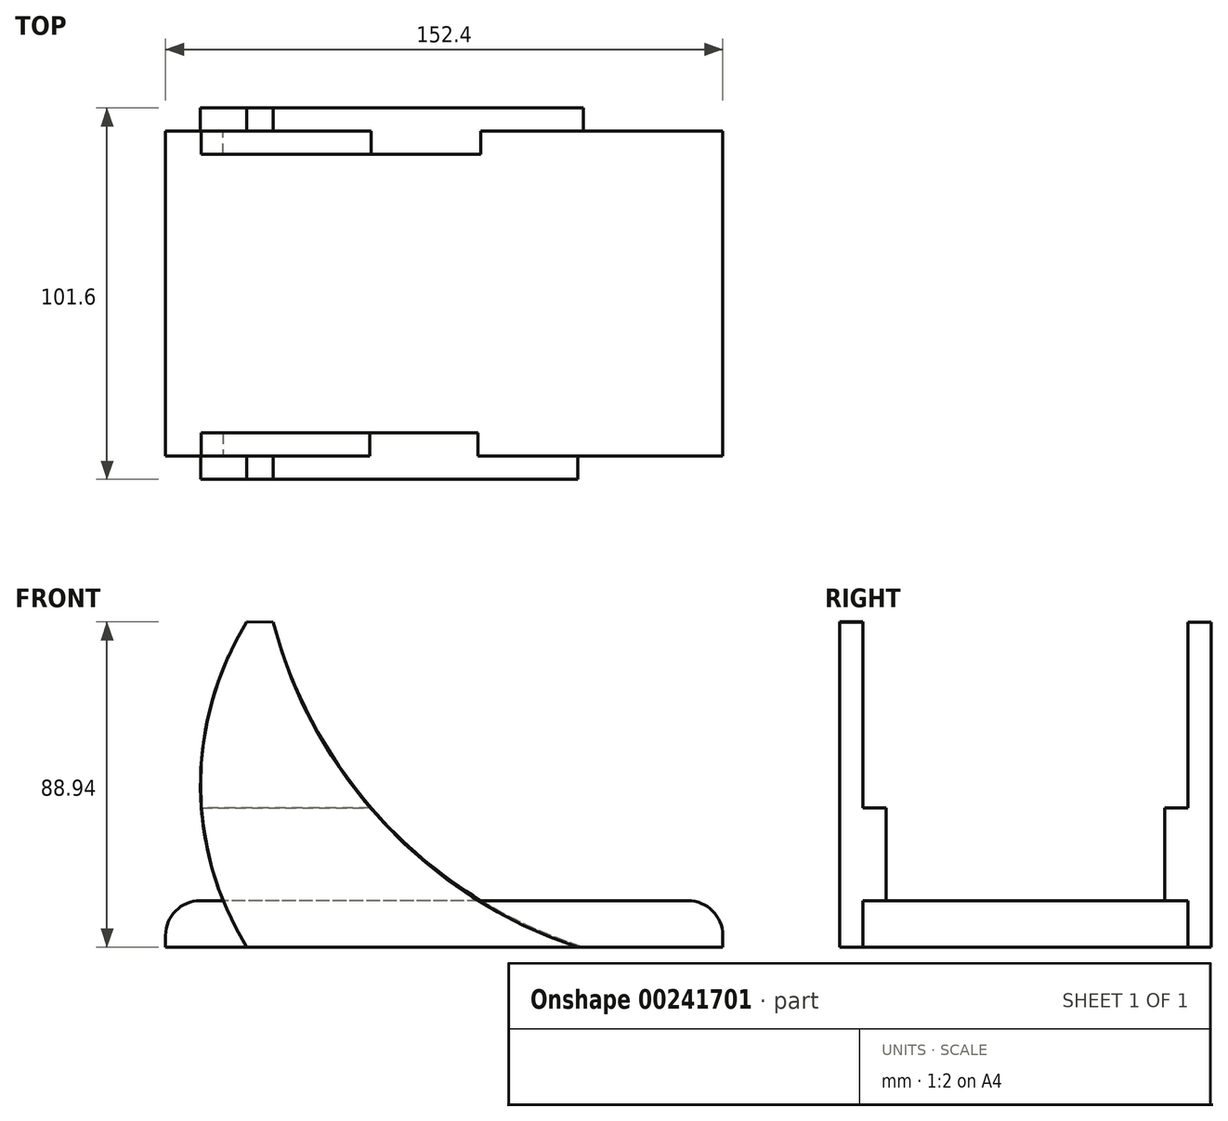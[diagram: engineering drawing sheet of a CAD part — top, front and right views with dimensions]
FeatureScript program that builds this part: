
annotation { "Feature Type Name" : "Feature", "Feature Type Description" : "" }
export const myFeature = defineFeature(function(context is Context, id is Id, definition is map)
    precondition{}
    {
        {
            var Q0;
            Q0=qCreatedBy(makeId("Top.planeOp"),FACE);
            var sketch = newSketch(context, id + "F0", { "sketchPlane" : qUnion([Q0])});
            skLineSegment(sketch, "E0.bottom", {"start": v(76.2, -44.45) * mm, "end": v(-76.2, -44.45) * mm});
            skLineSegment(sketch, "E0.top", {"start": v(76.2, 44.45) * mm, "end": v(-76.2, 44.45) * mm});
            skLineSegment(sketch, "E0.left", {"start": v(76.2, -44.45) * mm, "end": v(76.2, 44.45) * mm});
            skLineSegment(sketch, "E0.right", {"start": v(-76.2, -44.45) * mm, "end": v(-76.2, 44.45) * mm});
            skPoint(sketch, "E0.middle", {"position": v(0, 0) * mm});
            skSolve(sketch);
        }
        {
            var Q0;
            Q0=makeQuery(id+"F0.imprint","IMPRINT",FACE,{"disambiguationData":[TD([[makeQuery(id+"F0.imprint","IMPRINT",EDGE,{"derivedFrom":sQuery(id+"F0.wireOp",EDGE,"E0.bottom")}),-1.0]])]});
            extrude(context, id + "F1", {"entities" : qUnion([Q0]), "depth" : 12.7 * mm});
        }
        {
            var Q0;
            Q0=makeQuery(id+"F1.opExtrude","SWEPT_FACE",FACE,{"disambiguationData":[OSD([sQuery(id+"F0.wireOp",EDGE,"E0.bottom")])]});
            var sketch = newSketch(context, id + "F2", { "sketchPlane" : qUnion([Q0])});
            skArc(sketch, "E1", {"start": v(-53.95, 88.94) * mm, "mid": v(-66.64, 44.47) * mm, "end": v(-53.98, 0) * mm});
            skArc(sketch, "E2", {"start": v(-46.77, 88.9) * mm, "mid": v(-16.47, 33.8) * mm, "end": v(36.54, 0) * mm});
            skLineSegment(sketch, "E3", {"start": v(-53.95, 88.94) * mm, "end": v(-46.77, 88.9) * mm});
            skLineSegment(sketch, "E4", {"start": v(-53.98, 0) * mm, "end": v(36.54, 0) * mm});
            skPoint(sketch, "E5.endSnap0", {"position": v(0, 12.7) * mm});
            skLineSegment(sketch, "E6", {"start": v(-60.43, 12.7) * mm, "end": v(9.3, 12.7) * mm});
            skLineSegment(sketch, "E7", {"start": v(-20.31, 38.1) * mm, "end": v(-66.4, 38.1) * mm});
            skSolve(sketch);
        }
        {
            var Q0;
            Q0=makeQuery(id+"F1.opExtrude","CAP_EDGE",EDGE,{"disambiguationData":[OSD([sQuery(id+"F0.wireOp",EDGE,"E0.right")])],"isStart":false});
            fillet(context, id + "F3", {"entities" : qUnion([Q0]), "radius" : 9.52 * mm, "tangentPropagation" : true, "allowEdgeOverflow" : false});
        }
        {
            var Q0;
            Q0=makeQuery(id+"F1.opExtrude","CAP_EDGE",EDGE,{"disambiguationData":[OSD([sQuery(id+"F0.wireOp",EDGE,"E0.left")])],"isStart":false});
            fillet(context, id + "F4", {"entities" : qUnion([Q0]), "radius" : 9.52 * mm, "tangentPropagation" : true, "allowEdgeOverflow" : false});
        }
        {
            var Q0;
            Q0=makeQuery(id+"F1.opExtrude","SWEPT_FACE",FACE,{"disambiguationData":[OSD([sQuery(id+"F0.wireOp",EDGE,"E0.top")])]});
            var sketch = newSketch(context, id + "F5", { "sketchPlane" : qUnion([Q0])});
            skSolve(sketch);
        }
        {
            var Q0;
            {var subQ0=sQuery(id+"F2.wireOp",EDGE,"E3");Q0=makeQuery(id+"F2.imprint","IMPRINT",FACE,{"disambiguationData":[TD([[makeQuery(id+"F2.imprint","IMPRINT",EDGE,{"derivedFrom":subQ0}),-1.0]])]});}
            var Q1;
            {var subQ0=sQuery(id+"F2.wireOp",EDGE,"E6");Q1=makeQuery(id+"F2.imprint","IMPRINT",FACE,{"disambiguationData":[TD([[makeQuery(id+"F2.imprint","IMPRINT",EDGE,{"derivedFrom":subQ0}),-1.0]])]});}
            var Q2;
            {var subQ0=sQuery(id+"F2.wireOp",EDGE,"E4");Q2=makeQuery(id+"F2.imprint","IMPRINT",FACE,{"disambiguationData":[TD([[makeQuery(id+"F2.imprint","IMPRINT",EDGE,{"derivedFrom":subQ0}),-1.0]])]});}
            extrude(context, id + "F6", {"entities" : qUnion([Q0, Q1, Q2]), "depth" : 6.35 * mm});
        }
        {
            var Q0;
            {var subQ0=sQuery(id+"F2.wireOp",EDGE,"E6");Q0=makeQuery(id+"F2.imprint","IMPRINT",FACE,{"disambiguationData":[TD([[makeQuery(id+"F2.imprint","IMPRINT",EDGE,{"derivedFrom":subQ0}),-1.0]])]});}
            extrude(context, id + "F7", {"entities" : qUnion([Q0]), "operationType" : NewBodyOperationType.ADD, "oppositeDirection" : true, "depth" : 6.35 * mm});
        }
        {
            var Q0;
            {var subQ1=sQuery(id+"F0.wireOp",EDGE,"E0.top");Q0=makeQuery(id+"F5.imprint","IMPRINT",FACE,{"disambiguationData":[TD([[makeQuery(id+"F5.imprint","IMPRINT",EDGE,{"derivedFrom":makeQuery(id+"F1.opExtrude","CAP_EDGE",EDGE,{"disambiguationData":[OSD([subQ1])],"isStart":true})}),1.0]])]});}
            var sketch = newSketch(context, id + "F8", { "sketchPlane" : qUnion([Q0])});
            skLineSegment(sketch, "E8", {"start": v(-76.22, 0) * mm, "end": v(-38.12, 0) * mm});
            skArc(sketch, "E9", {"start": v(-38.12, 0) * mm, "mid": v(15.79, 33.5) * mm, "end": v(46.75, 88.9) * mm});
            skArc(sketch, "E10", {"start": v(53.96, 0) * mm, "mid": v(66.66, 44.45) * mm, "end": v(53.96, 88.9) * mm});
            skLineSegment(sketch, "E11", {"start": v(46.75, 88.9) * mm, "end": v(53.96, 88.9) * mm});
            skLineSegment(sketch, "E12", {"start": v(-38.12, 0) * mm, "end": v(53.96, 0) * mm});
            skLineSegment(sketch, "E13", {"start": v(66.42, 38.1) * mm, "end": v(19.97, 38.1) * mm});
            skLineSegment(sketch, "E14", {"start": v(-10.06, 12.7) * mm, "end": v(60.44, 12.7) * mm});
            skSolve(sketch);
        }
        {
            var Q0;
            {var subQ0=sQuery(id+"F8.wireOp",EDGE,"E11");Q0=makeQuery(id+"F8.imprint","IMPRINT",FACE,{"disambiguationData":[TD([[makeQuery(id+"F8.imprint","IMPRINT",EDGE,{"derivedFrom":subQ0}),-1.0]])]});}
            var Q1;
            {var subQ0=sQuery(id+"F8.wireOp",EDGE,"E13");Q1=makeQuery(id+"F8.imprint","IMPRINT",FACE,{"disambiguationData":[TD([[makeQuery(id+"F8.imprint","IMPRINT",EDGE,{"derivedFrom":subQ0}),1.0]])]});}
            var Q2;
            {var subQ0=sQuery(id+"F8.wireOp",EDGE,"E12");Q2=makeQuery(id+"F8.imprint","IMPRINT",FACE,{"disambiguationData":[TD([[makeQuery(id+"F8.imprint","IMPRINT",EDGE,{"derivedFrom":subQ0}),1.0]])]});}
            extrude(context, id + "F9", {"entities" : qUnion([Q0, Q1, Q2]), "depth" : 6.35 * mm});
        }
        {
            var Q0;
            {var subQ0=sQuery(id+"F8.wireOp",EDGE,"E13");Q0=makeQuery(id+"F8.imprint","IMPRINT",FACE,{"disambiguationData":[TD([[makeQuery(id+"F8.imprint","IMPRINT",EDGE,{"derivedFrom":subQ0}),1.0]])]});}
            extrude(context, id + "F10", {"entities" : qUnion([Q0]), "operationType" : NewBodyOperationType.ADD, "oppositeDirection" : true, "depth" : 6.35 * mm});
        }
    });
